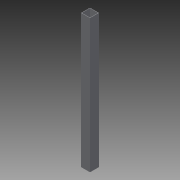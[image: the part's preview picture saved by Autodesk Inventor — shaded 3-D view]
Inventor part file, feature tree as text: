
AUTODESK INVENTOR PART (.ipt)
format: ipt  version: 2015 (Build 190159000, 159)  size: 73,728 bytes
history: native  units: in
note: dims shown in document units (in); Inventor stores cm internally (conversion verified against a paired STEP export)
features: extrude x1, sketch x1
ambient origin geometry x8: Origin, YZ Plane, XZ Plane, XY Plane, X Axis, Y Axis, Z Axis, Center Point
bodies: Solid1 (feature_tree)
feature tree (2):
  extrude  "Extrusion1"  Depth=2.0in
  sketch  "Sketch1"  dims[d0=2.0in d1=2.0in d2=0.083in d3=30.0in d4=0.0in]
